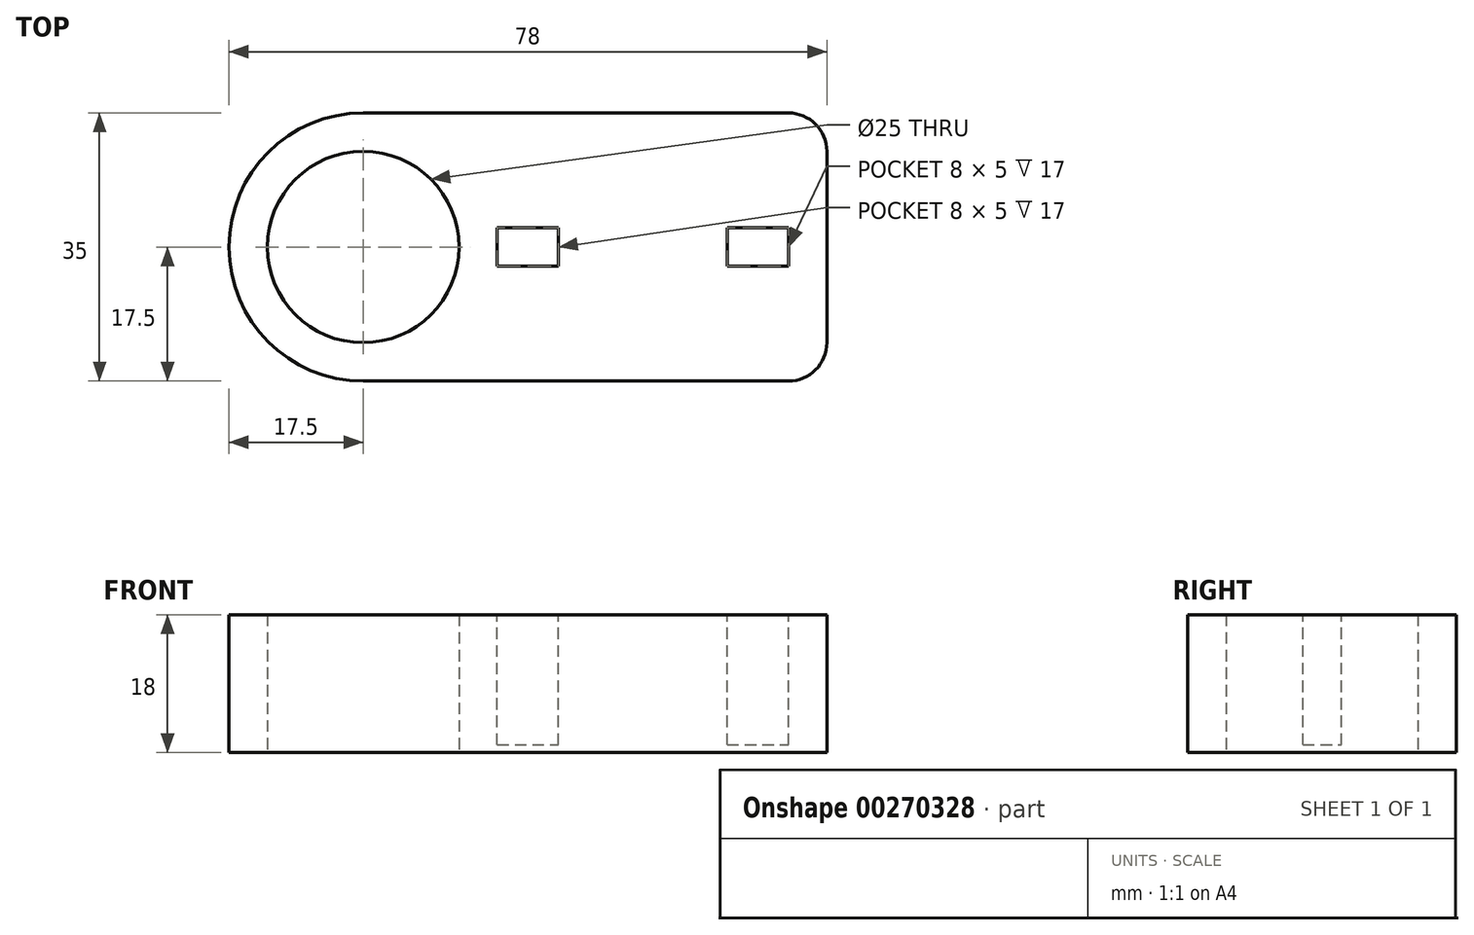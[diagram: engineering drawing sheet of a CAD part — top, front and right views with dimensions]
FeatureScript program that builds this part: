
annotation { "Feature Type Name" : "Feature", "Feature Type Description" : "" }
export const myFeature = defineFeature(function(context is Context, id is Id, definition is map)
    precondition{}
    {
        {
            var Q0;
            Q0=qCreatedBy(makeId("Top.planeOp"),FACE);
            var sketch = newSketch(context, id + "F0", { "sketchPlane" : qUnion([Q0])});
            skLineSegment(sketch, "E0.bottom", {"start": v(17.5, 0) * mm, "end": v(73, 0) * mm});
            skLineSegment(sketch, "E0.top", {"start": v(17.5, 35) * mm, "end": v(73, 35) * mm});
            skLineSegment(sketch, "E0.left", {"start": v(0, 17.5) * mm, "end": v(0, 17.5) * mm});
            skLineSegment(sketch, "E0.right", {"start": v(78, 5) * mm, "end": v(78, 30) * mm});
            skLineSegment(sketch, "E1.bottom", {"start": v(0, 0) * mm, "end": v(17.5, 0) * mm, "construction": true});
            skLineSegment(sketch, "E1.top", {"start": v(0, 17.5) * mm, "end": v(17.5, 17.5) * mm, "construction": true});
            skLineSegment(sketch, "E1.left", {"start": v(0, 0) * mm, "end": v(0, 17.5) * mm, "construction": true});
            skLineSegment(sketch, "E1.right", {"start": v(17.5, 0) * mm, "end": v(17.5, 17.5) * mm, "construction": true});
            skCircle(sketch, "E2", {"center": v(17.5, 17.5) * mm, "radius": 12.5 * mm});
            skPoint(sketch, "E3.visualSharp", {"position": v(0, 0) * mm});
            skArc(sketch, "E3.filletArc", {"start": v(0, 17.5) * mm, "mid": v(5.13, 5.13) * mm, "end": v(17.5, 0) * mm});
            skPoint(sketch, "E4.visualSharp", {"position": v(0, 35) * mm});
            skArc(sketch, "E4.filletArc", {"start": v(17.5, 35) * mm, "mid": v(5.13, 29.87) * mm, "end": v(0, 17.5) * mm});
            skPoint(sketch, "E5.visualSharp", {"position": v(78, 35) * mm});
            skArc(sketch, "E5.filletArc", {"start": v(78, 30) * mm, "mid": v(76.54, 33.54) * mm, "end": v(73, 35) * mm});
            skPoint(sketch, "E6.visualSharp", {"position": v(78, 0) * mm});
            skArc(sketch, "E6.filletArc", {"start": v(73, 0) * mm, "mid": v(76.54, 1.46) * mm, "end": v(78, 5) * mm});
            skSolve(sketch);
        }
        {
            var Q0;
            Q0=makeQuery(id+"F0.imprint","IMPRINT",FACE,{"disambiguationData":[TD([[makeQuery(id+"F0.imprint","IMPRINT",EDGE,{"derivedFrom":sQuery(id+"F0.wireOp",EDGE,"E0.bottom")}),1.0]])]});
            extrude(context, id + "F1", {"entities" : qUnion([Q0]), "depth" : 18 * mm});
        }
        {
            var Q0;
            Q0=makeQuery(id+"F1.opExtrude","CAP_FACE",FACE,{"disambiguationData":[OSD([sQuery(id+"F0.wireOp",EDGE,"E0.bottom"),sQuery(id+"F0.wireOp",EDGE,"E0.top"),sQuery(id+"F0.wireOp",EDGE,"E0.right"),sQuery(id+"F0.wireOp",EDGE,"E2"),sQuery(id+"F0.wireOp",EDGE,"E3.filletArc"),sQuery(id+"F0.wireOp",EDGE,"E4.filletArc"),sQuery(id+"F0.wireOp",EDGE,"E5.filletArc"),sQuery(id+"F0.wireOp",EDGE,"E6.filletArc")])],"isStart":false});
            var sketch = newSketch(context, id + "F2", { "sketchPlane" : qUnion([Q0])});
            skLineSegment(sketch, "E7.bottom", {"start": v(0, 0) * mm, "end": v(35, 0) * mm, "construction": true});
            skLineSegment(sketch, "E7.top", {"start": v(0, 15) * mm, "end": v(35, 15) * mm, "construction": true});
            skLineSegment(sketch, "E7.left", {"start": v(0, 0) * mm, "end": v(0, 15) * mm, "construction": true});
            skLineSegment(sketch, "E7.right", {"start": v(35, 0) * mm, "end": v(35, 15) * mm, "construction": true});
            skLineSegment(sketch, "E8.bottom", {"start": v(35, 15) * mm, "end": v(43, 15) * mm});
            skLineSegment(sketch, "E8.top", {"start": v(35, 20) * mm, "end": v(43, 20) * mm});
            skLineSegment(sketch, "E8.left", {"start": v(35, 15) * mm, "end": v(35, 20) * mm});
            skLineSegment(sketch, "E8.right", {"start": v(43, 15) * mm, "end": v(43, 20) * mm});
            skLineSegment(sketch, "E9", {"start": v(43, 15) * mm, "end": v(65, 15) * mm, "construction": true});
            skLineSegment(sketch, "E10.bottom", {"start": v(65, 15) * mm, "end": v(73, 15) * mm});
            skLineSegment(sketch, "E10.top", {"start": v(65, 20) * mm, "end": v(73, 20) * mm});
            skLineSegment(sketch, "E10.left", {"start": v(65, 15) * mm, "end": v(65, 20) * mm});
            skLineSegment(sketch, "E10.right", {"start": v(73, 15) * mm, "end": v(73, 20) * mm});
            skSolve(sketch);
        }
        {
            var Q0;
            Q0 = qSketchRegion(id + "F2", true);
            extrude(context, id + "F3", {"entities" : qUnion([Q0]), "operationType" : NewBodyOperationType.REMOVE, "oppositeDirection" : true, "depth" : 17 * mm});
        }
    });
